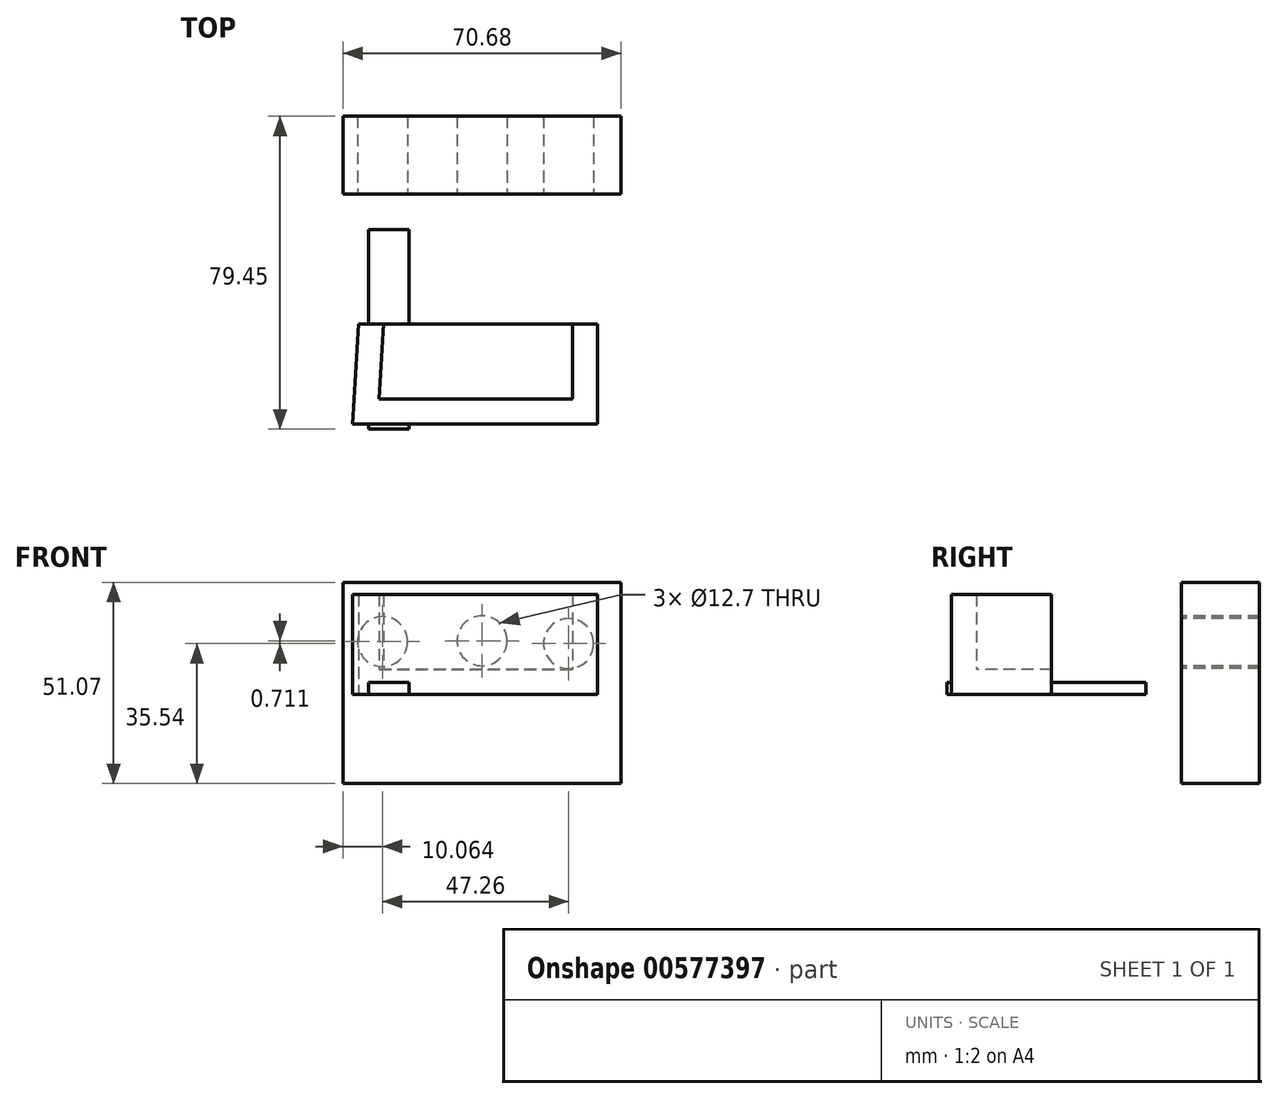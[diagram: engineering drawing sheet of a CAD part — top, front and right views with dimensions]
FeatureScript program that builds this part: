
annotation { "Feature Type Name" : "Feature", "Feature Type Description" : "" }
export const myFeature = defineFeature(function(context is Context, id is Id, definition is map)
    precondition{}
    {
        {
            var Q0;
            Q0=qCreatedBy(makeId("Front.planeOp"),FACE);
            var sketch = newSketch(context, id + "F0", { "sketchPlane" : qUnion([Q0])});
            skLineSegment(sketch, "E0", {"start": v(-43.17, 28.46) * mm, "end": v(-43.17, -22.61) * mm});
            skLineSegment(sketch, "E1", {"start": v(-43.17, -22.61) * mm, "end": v(27.51, -22.61) * mm});
            skLineSegment(sketch, "E2", {"start": v(27.51, -22.61) * mm, "end": v(27.51, 28.46) * mm});
            skLineSegment(sketch, "E3", {"start": v(27.51, 28.46) * mm, "end": v(-43.17, 28.46) * mm});
            skSolve(sketch);
        }
        {
            var Q0;
            Q0 = qSketchRegion(id + "F0", true);
            extrude(context, id + "F1", {"entities" : qUnion([Q0]), "depth" : 19.8 * mm, "offsetDistance" : 25.4 * mm});
        }
        {
            var Q0;
            Q0=makeQuery(id+"F1.opExtrude","CAP_FACE",FACE,{"disambiguationData":[OSD([sQuery(id+"F0.wireOp",EDGE,"E0"),sQuery(id+"F0.wireOp",EDGE,"E1"),sQuery(id+"F0.wireOp",EDGE,"E2"),sQuery(id+"F0.wireOp",EDGE,"E3")])],"isStart":false});
            var sketch = newSketch(context, id + "F2", { "sketchPlane" : qUnion([Q0])});
            skPoint(sketch, "E4", {"position": v(-33.1, 13.43) * mm});
            skPoint(sketch, "E5", {"position": v(18.92, 13.43) * mm});
            skSolve(sketch);
        }
        {
            var Q0;
            Q0=sQuery(id+"F2.wireOp",VERTEX,"E4");
            var Q1;
            Q1=makeQuery(id+"F1.opExtrude","SWEPT_BODY",BODY,{"disambiguationData":[OSD([sQuery(id+"F0.wireOp",EDGE,"E0"),sQuery(id+"F0.wireOp",EDGE,"E1"),sQuery(id+"F0.wireOp",EDGE,"E2"),sQuery(id+"F0.wireOp",EDGE,"E3")])]});
            hole(context, id + "F3", {"style" : HoleStyle.SIMPLE, "endStyle" : HoleEndStyle.THROUGH, "holeDiameter" : 12.7 * mm, "isTappedThrough" : true, "tappedDepth" : 12.7 * mm, "tapClearance" : 3, "locations" : qUnion([Q0]), "scope" : qUnion([Q1])});
        }
        {
            var Q0;
            Q0=makeQuery(id+"F1.opExtrude","CAP_FACE",FACE,{"disambiguationData":[OSD([sQuery(id+"F0.wireOp",EDGE,"E0"),sQuery(id+"F0.wireOp",EDGE,"E1"),sQuery(id+"F0.wireOp",EDGE,"E2"),sQuery(id+"F0.wireOp",EDGE,"E3")])],"isStart":false});
            var sketch = newSketch(context, id + "F4", { "sketchPlane" : qUnion([Q0])});
            skPoint(sketch, "E6", {"position": v(14.15, 12.93) * mm});
            skSolve(sketch);
        }
        {
            var Q0;
            Q0=sQuery(id+"F4.wireOp",VERTEX,"E6");
            var Q1;
            Q1=makeQuery(id+"F1.opExtrude","SWEPT_BODY",BODY,{"disambiguationData":[OSD([sQuery(id+"F0.wireOp",EDGE,"E0"),sQuery(id+"F0.wireOp",EDGE,"E1"),sQuery(id+"F0.wireOp",EDGE,"E2"),sQuery(id+"F0.wireOp",EDGE,"E3")])]});
            hole(context, id + "F5", {"style" : HoleStyle.SIMPLE, "endStyle" : HoleEndStyle.THROUGH, "holeDiameter" : 12.7 * mm, "isTappedThrough" : true, "tappedDepth" : 12.7 * mm, "tapClearance" : 3, "locations" : qUnion([Q0]), "scope" : qUnion([Q1])});
        }
        {
            var Q0;
            Q0=makeQuery(id+"F1.opExtrude","CAP_FACE",FACE,{"disambiguationData":[OSD([sQuery(id+"F0.wireOp",EDGE,"E0"),sQuery(id+"F0.wireOp",EDGE,"E1"),sQuery(id+"F0.wireOp",EDGE,"E2"),sQuery(id+"F0.wireOp",EDGE,"E3")])],"isStart":false});
            var sketch = newSketch(context, id + "F6", { "sketchPlane" : qUnion([Q0])});
            skPoint(sketch, "E7", {"position": v(-7.83, 13.64) * mm});
            skPoint(sketch, "E7.positionSnap0", {"position": v(-7.83, 28.46) * mm});
            skSolve(sketch);
        }
        {
            var Q0;
            Q0=sQuery(id+"F6.wireOp",VERTEX,"E7");
            var Q1;
            Q1=makeQuery(id+"F1.opExtrude","SWEPT_BODY",BODY,{"disambiguationData":[OSD([sQuery(id+"F0.wireOp",EDGE,"E0"),sQuery(id+"F0.wireOp",EDGE,"E1"),sQuery(id+"F0.wireOp",EDGE,"E2"),sQuery(id+"F0.wireOp",EDGE,"E3")])]});
            hole(context, id + "F7", {"style" : HoleStyle.SIMPLE, "endStyle" : HoleEndStyle.THROUGH, "holeDiameter" : 12.7 * mm, "isTappedThrough" : true, "tappedDepth" : 12.7 * mm, "tapClearance" : 3, "locations" : qUnion([Q0]), "scope" : qUnion([Q1])});
        }
        {
            var Q0;
            Q0=qCreatedBy(makeId("Top.planeOp"),FACE);
            var sketch = newSketch(context, id + "F8", { "sketchPlane" : qUnion([Q0])});
            skLineSegment(sketch, "E8", {"start": v(-40.73, -78.2) * mm, "end": v(21.53, -78.2) * mm});
            skLineSegment(sketch, "E9", {"start": v(21.53, -78.2) * mm, "end": v(21.53, -52.83) * mm});
            skLineSegment(sketch, "E10", {"start": v(21.53, -52.83) * mm, "end": v(-39.18, -52.83) * mm});
            skLineSegment(sketch, "E11", {"start": v(-39.18, -52.83) * mm, "end": v(-40.73, -78.2) * mm});
            skSolve(sketch);
        }
        {
            var Q0;
            Q0=makeQuery(id+"F8.imprint","IMPRINT",FACE,{"disambiguationData":[TD([[makeQuery(id+"F8.imprint","IMPRINT",EDGE,{"derivedFrom":sQuery(id+"F8.wireOp",EDGE,"E8")}),1.0]])]});
            extrude(context, id + "F9", {"entities" : qUnion([Q0]), "depth" : 25.4 * mm, "offsetDistance" : 25.4 * mm});
        }
        {
            var Q0;
            Q0=makeQuery(id+"F9.opExtrude","SWEPT_FACE",FACE,{"disambiguationData":[OSD([sQuery(id+"F8.wireOp",EDGE,"E10")])]});
            var Q1;
            Q1=makeQuery(id+"F9.opExtrude","CAP_FACE",FACE,{"disambiguationData":[OSD([sQuery(id+"F8.wireOp",EDGE,"E8"),sQuery(id+"F8.wireOp",EDGE,"E9"),sQuery(id+"F8.wireOp",EDGE,"E10"),sQuery(id+"F8.wireOp",EDGE,"E11")])],"isStart":false});
            shell(context, id + "F10", {"entities" : qUnion([Q0, Q1]), "thickness" : 6.35 * mm});
        }
        {
            var Q0;
            Q0=qCreatedBy(makeId("Top.planeOp"),FACE);
            var sketch = newSketch(context, id + "F11", { "sketchPlane" : qUnion([Q0])});
            skLineSegment(sketch, "E12", {"start": v(-36.64, -79.45) * mm, "end": v(-36.64, -28.83) * mm});
            skLineSegment(sketch, "E13", {"start": v(-36.64, -28.83) * mm, "end": v(-26.44, -28.83) * mm});
            skLineSegment(sketch, "E14", {"start": v(-26.44, -28.83) * mm, "end": v(-26.44, -79.45) * mm});
            skLineSegment(sketch, "E15", {"start": v(-26.44, -79.45) * mm, "end": v(-36.64, -79.45) * mm});
            skSolve(sketch);
        }
        {
            var Q0;
            Q0 = qSketchRegion(id + "F11", true);
            extrude(context, id + "F12", {"entities" : qUnion([Q0]), "operationType" : NewBodyOperationType.ADD, "depth" : 3.05 * mm, "offsetDistance" : 25.4 * mm});
        }
    });
